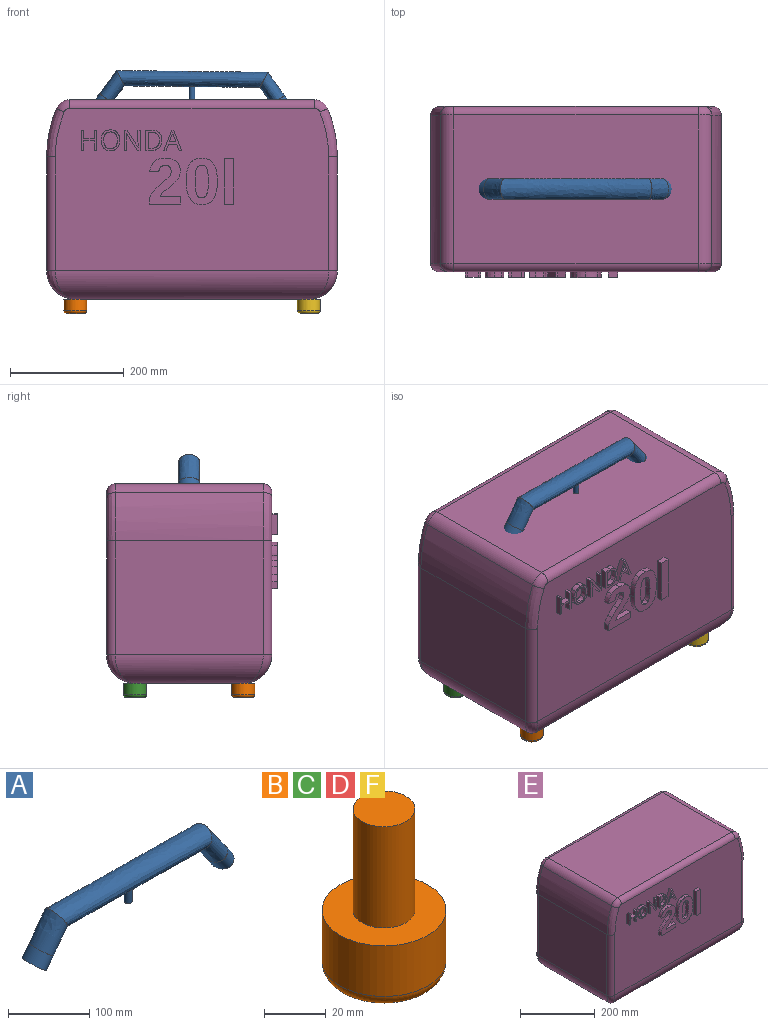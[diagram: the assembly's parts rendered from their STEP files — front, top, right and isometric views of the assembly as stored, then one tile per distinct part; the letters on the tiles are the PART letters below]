
ASSEMBLY  parts=6 mates=5
PART A: 9 faces, bbox 359.2x36.4x84.2 mm
  f0: bspline ~265.3x36.21mm, area 25120.1mm2, adj f3,f5,f7
  f1: plane 36.39x21.71mm, normal (0.59,0,-0.81), area 769.4mm2, adj f4
  f2: plane 36.39x21.24mm, normal (-0.61,0,-0.79), area 769.4mm2, adj f6
  f3: bspline ~56.62x50.7mm, area 4362mm2, adj f0,f4
  f4: bspline ~55.05x48.1mm, area 2003.3mm2, adj f1,f3
  f5: bspline ~56.89x52.04mm, area 4384.8mm2, adj f0,f6
  f6: bspline ~36.21x33.59mm, area 2002mm2, adj f2,f5
  f7: cylinder r=5mm len=23.14mm, axis (0,0,-1), area 727mm2, adj f0,f8
  f8: plane 10x10mm, normal (0,0,-1), area 78.5mm2, adj f7
PART B: 6 faces, bbox 43.3x43.3x65 mm
  f0: cylinder r=20mm len=40mm, axis (0,0,1), area 2513.3mm2, adj f2,f5
  f1: plane 30x30mm, normal (0,0,-1), area 706.9mm2, adj f5
  f2: plane 40x40mm, normal (0,0,1), area 942.5mm2, adj f0,f3
  f3: cylinder r=10mm len=40mm, axis (0,0,-1), area 2513.3mm2, adj f2,f4
  f4: plane 20x20mm, normal (0,0,1), area 314.2mm2, adj f3
  f5: torus R=15mm, axis (0,0,1), area 897.3mm2, adj f0,f1
PART C: same geometry as B
PART D: same geometry as B
PART E: 160 faces, bbox 510x300x350 mm
  f0: plane 260x200mm, normal (1,0,0), area 52000mm2, adj f3,f6,f15,f30
  f1: plane 429.9x260mm, normal (0,0,1), area 111772.7mm2, adj f10,f11,f18,f27
  f2: plane 260x200mm, normal (-1,0,0), area 52000mm2, adj f4,f7,f21,f24
  f3: extruded ~260x84.59mm, area 22577.4mm2, adj f0,f10,f16,f29
  f4: extruded ~260x84.59mm, area 22577.4mm2, adj f2,f11,f20,f25
  f5: plane 410x190mm, normal (0,0,-1), area 77900mm2, adj f6,f7,f9,f13
  f6: cylinder r=50mm len=260mm, axis (0,-1,0), area 18422.6mm2, adj f0,f5,f14,f31
  f7: cylinder r=50mm len=260mm, axis (0,1,0), area 18422.6mm2, adj f2,f5,f22,f23
  f8: plane 480x285mm, normal (0,1,0), area 135753.4mm2, adj f9,f24,f25,f26,f27,f28,f29,f30
  f9: cylinder r=50mm len=480mm, axis (1,0,0), area 35701.3mm2, adj f5,f8,f23,f31
  f10: cylinder r=25mm len=260mm, axis (0,1,0), area 7651mm2, adj f1,f3,f17,f28
  f11: cylinder r=25mm len=260mm, axis (0,1,0), area 7651mm2, adj f1,f4,f19,f26
  f12: plane 480x285mm, normal (0,-1,0), area 125242.9mm2, adj f13,f15,f16,f17,f18,f19,f20,f21
  f13: cylinder r=50mm len=480mm, axis (1,0,0), area 35701.3mm2, adj f5,f12,f14,f22
  f14: bspline ~58.44x50mm, area 1261.4mm2, adj f6,f13,f15
  f15: cylinder r=15mm len=200mm, axis (0,0,1), area 4712.4mm2, adj f0,f12,f14,f16
  f16: bspline ~109.39x35.94mm, area 1995.5mm2, adj f3,f12,f15,f17
  f17: torus R=10mm, axis (0,1,0), area 542.2mm2, adj f10,f12,f16,f18
  f18: cylinder r=15mm len=429.9mm, axis (-1,0,0), area 10129.2mm2, adj f1,f12,f17,f19
  f19: torus R=10mm, axis (0,1,0), area 542.2mm2, adj f11,f12,f18,f20
  f20: bspline ~109.39x35.94mm, area 1995.5mm2, adj f4,f12,f19,f21
  f21: cylinder r=15mm len=200mm, axis (0,0,-1), area 4712.4mm2, adj f2,f12,f20,f22
  f22: bspline ~58.44x50mm, area 1261.4mm2, adj f7,f13,f21
  f23: bspline ~58.44x50mm, area 1261.4mm2, adj f7,f9,f24
  f24: cylinder r=15mm len=200mm, axis (0,0,-1), area 4712.4mm2, adj f2,f8,f23,f25
  f25: bspline ~109.39x35.94mm, area 1995.5mm2, adj f4,f8,f24,f26
  f26: torus R=10mm, axis (0,-1,0), area 542.2mm2, adj f8,f11,f25,f27
  f27: cylinder r=15mm len=429.9mm, axis (-1,0,0), area 10129.2mm2, adj f1,f8,f26,f28
  f28: torus R=10mm, axis (0,-1,0), area 542.2mm2, adj f8,f10,f27,f29
  f29: bspline ~109.39x35.94mm, area 1995.5mm2, adj f3,f8,f28,f30
  f30: cylinder r=15mm len=200mm, axis (0,0,1), area 4712.4mm2, adj f0,f8,f29,f31
  f31: bspline ~58.44x50mm, area 1261.4mm2, adj f6,f9,f30
  f32: plane 35.58x10mm, normal (1,0,0), area 355.8mm2, adj f12,f33,f43,f44
  f33: plane 10x4.14mm, normal (0,0,1), area 41.4mm2, adj f12,f32,f34,f44
  f34: plane 15.14x10mm, normal (-1,0,0), area 151.4mm2, adj f12,f33,f35,f44
  f35: plane 18.74x10mm, normal (0,0,1), area 187.4mm2, adj f12,f34,f36,f44
  f36: plane 15.14x10mm, normal (1,0,0), area 151.4mm2, adj f12,f35,f37,f44
  f37: plane 10x4.14mm, normal (0,0,1), area 41.4mm2, adj f12,f36,f38,f44
  f38: plane 35.58x10mm, normal (-1,0,0), area 355.8mm2, adj f12,f37,f39,f44
  f39: plane 10x4.14mm, normal (0,0,-1), area 41.4mm2, adj f12,f38,f40,f44
  f40: plane 16.74x10mm, normal (1,0,0), area 167.4mm2, adj f12,f39,f41,f44
  f41: plane 18.74x10mm, normal (0,0,-1), area 187.4mm2, adj f12,f40,f42,f44
  f42: plane 16.74x10mm, normal (-1,0,0), area 167.4mm2, adj f12,f41,f43,f44
  f43: plane 10x4.14mm, normal (0,0,-1), area 41.4mm2, adj f12,f32,f42,f44
  f44: plane 35.58x27.01mm, normal (0,-1,0), area 363.6mm2, adj f32,f33,f34,f35,f36,f37,f38,f39
  f45: extruded ~13.43x10mm, area 144.3mm2, adj f12,f46,f60,f61
  f46: extruded ~11.98x10mm, area 133.5mm2, adj f12,f45,f47,f61
  f47: extruded ~12.16x10mm, area 134.9mm2, adj f12,f46,f48,f61
  f48: extruded ~13.47x10mm, area 144.6mm2, adj f12,f47,f49,f61
  f49: extruded ~13.57x10mm, area 145.5mm2, adj f12,f48,f50,f61
  f50: extruded ~12.13x10mm, area 134.7mm2, adj f12,f49,f51,f61
  f51: extruded ~12.01x10mm, area 133.9mm2, adj f12,f50,f60,f61
  f52: extruded ~10.86x10mm, area 115.2mm2, adj f53,f59,f61,f62
  f53: extruded ~10x8.99mm, area 100.8mm2, adj f52,f54,f61,f62
  f54: extruded ~10x8.89mm, area 99.8mm2, adj f53,f55,f61,f62
  f55: extruded ~10.89x10mm, area 115.2mm2, adj f54,f56,f61,f62
  f56: extruded ~10.98x10mm, area 116.1mm2, adj f55,f57,f61,f62
  f57: extruded ~10x8.93mm, area 100.2mm2, adj f56,f58,f61,f62
  f58: extruded ~10x8.94mm, area 100.4mm2, adj f57,f59,f61,f62
  f59: extruded ~10.96x10mm, area 116.1mm2, adj f52,f58,f61,f62
  f60: extruded ~13.44x10mm, area 144.4mm2, adj f12,f45,f51,f61
  f61: plane 36.63x32.73mm, normal (0,-1,0), area 400.6mm2, adj f45,f46,f47,f48,f49,f50,f51,f52
  f62: plane 29.3x23.97mm, normal (0,-1,0), area 582.3mm2, adj f52,f53,f54,f55,f56,f57,f58,f59
  f63: plane 35.58x10mm, normal (1,0,0), area 355.8mm2, adj f12,f64,f77,f78
  f64: plane 10x3.87mm, normal (0,0,1), area 38.7mm2, adj f12,f63,f65,f78
  f65: plane 20.42x10mm, normal (-1,0,0), area 204.2mm2, adj f12,f64,f66,f78
  f66: extruded ~10x5.1mm, area 51mm2, adj f12,f65,f67,f78
  f67: extruded ~10x4.22mm, area 42.3mm2, adj f12,f66,f68,f78
  f68: plane 10x0.19mm, normal (0,0,1), area 1.9mm2, adj f12,f67,f69,f78
  f69: plane 29.74x19.4mm, normal (0.84,0,0.55), area 355.1mm2, adj f12,f68,f70,f78
  f70: plane 10x4.67mm, normal (0,0,1), area 46.7mm2, adj f12,f69,f71,f78
  f71: plane 35.58x10mm, normal (-1,0,0), area 355.8mm2, adj f12,f70,f72,f78
  f72: plane 10x3.82mm, normal (0,0,-1), area 38.2mm2, adj f12,f71,f73,f78
  f73: plane 20.22x10mm, normal (1,0,0), area 202.2mm2, adj f12,f72,f74,f78
  f74: extruded ~10x9.63mm, area 96.4mm2, adj f12,f73,f75,f78
  f75: plane 10x0.19mm, normal (0,0,-1), area 1.9mm2, adj f12,f74,f76,f78
  f76: plane 29.86x19.45mm, normal (-0.84,0,-0.55), area 356.3mm2, adj f12,f75,f77,f78
  f77: plane 10x4.72mm, normal (0,0,-1), area 47.2mm2, adj f12,f63,f76,f78
  f78: plane 35.58x27.79mm, normal (0,-1,0), area 417.9mm2, adj f63,f64,f65,f66,f67,f68,f69,f70
  f79: extruded ~12.85x10mm, area 140.2mm2, adj f12,f80,f92,f93
  f80: extruded ~12.9x10mm, area 140.7mm2, adj f12,f79,f81,f93
  f81: plane 10.9x10mm, normal (0,0,1), area 109mm2, adj f12,f80,f82,f93
  f82: plane 35.58x10mm, normal (-1,0,0), area 355.8mm2, adj f12,f81,f83,f93
  f83: plane 10x9.86mm, normal (0,0,-1), area 98.6mm2, adj f12,f82,f84,f93
  f84: extruded ~13.76x10mm, area 149.1mm2, adj f12,f83,f92,f93
  f85: extruded ~10.77x10mm, area 117.1mm2, adj f86,f91,f93,f94
  f86: extruded ~11.12x10mm, area 120.1mm2, adj f85,f87,f93,f94
  f87: plane 10x5.04mm, normal (0,0,1), area 50.4mm2, adj f86,f88,f93,f94
  f88: plane 28.42x10mm, normal (1,0,0), area 284.2mm2, adj f87,f89,f93,f94
  f89: plane 10x6.01mm, normal (0,0,-1), area 60.1mm2, adj f88,f90,f93,f94
  f90: extruded ~10.38x10mm, area 112.6mm2, adj f89,f91,f93,f94
  f91: extruded ~10.49x10mm, area 113.5mm2, adj f85,f90,f93,f94
  f92: extruded ~13.47x10mm, area 146.9mm2, adj f12,f79,f84,f93
  f93: plane 35.58x28.4mm, normal (0,-1,0), area 400.4mm2, adj f79,f80,f81,f82,f83,f84,f85,f86
  f94: plane 28.42x19.89mm, normal (0,-1,0), area 496.5mm2, adj f85,f86,f87,f88,f89,f90,f91
  f95: plane 10x4.28mm, normal (0,0,-1), area 42.8mm2, adj f12,f96,f107,f108
  f96: plane 35.73x13.99mm, normal (0.93,0,0.36), area 383.7mm2, adj f12,f95,f97,f108
  f97: plane 10x3.48mm, normal (0,0,1), area 34.8mm2, adj f12,f96,f98,f108
  f98: plane 35.73x14.06mm, normal (-0.93,0,0.37), area 384mm2, adj f12,f97,f99,f108
  f99: plane 10x4.19mm, normal (0,0,-1), area 41.9mm2, adj f12,f98,f100,f108
  f100: plane 11.32x10mm, normal (0.93,0,-0.36), area 121.3mm2, adj f12,f99,f101,f108
  f101: plane 14.26x10mm, normal (0,0,-1), area 142.6mm2, adj f12,f100,f107,f108
  f102: plane 11.51x10mm, normal (0,0,1), area 115.1mm2, adj f103,f106,f108,f109
  f103: plane 11.03x10mm, normal (0.94,0,-0.35), area 117.9mm2, adj f102,f104,f108,f109
  f104: extruded ~10x5.13mm, area 53.6mm2, adj f103,f105,f108,f109
  f105: extruded ~10x5.13mm, area 53.9mm2, adj f104,f106,f108,f109
  f106: plane 11.03x10mm, normal (-0.94,0,-0.35), area 117.8mm2, adj f102,f105,f108,f109
  f107: plane 11.32x10mm, normal (-0.93,0,-0.36), area 121.5mm2, adj f12,f95,f101,f108
  f108: plane 35.73x31.54mm, normal (0,-1,0), area 325.7mm2, adj f95,f96,f97,f98,f99,f100,f101,f102
  f109: plane 16.16x11.51mm, normal (0,-1,0), area 88.7mm2, adj f102,f103,f104,f105,f106
  f110: plane 55.43x10mm, normal (0,0,-1), area 554.3mm2, adj f12,f111,f131,f132
  f111: plane 12.99x10mm, normal (1,0,0), area 129.9mm2, adj f12,f110,f112,f132
  f112: plane 36.77x10mm, normal (0,0,1), area 367.7mm2, adj f12,f111,f113,f132
  f113: extruded ~10x6.85mm, area 84.3mm2, adj f12,f112,f114,f132
  f114: extruded ~10x7.17mm, area 95.8mm2, adj f12,f113,f115,f132
  f115: extruded ~10x8.12mm, area 103.8mm2, adj f12,f114,f116,f132
  f116: extruded ~10x7.62mm, area 104.4mm2, adj f12,f115,f117,f132
  f117: extruded ~10x8.29mm, area 100.5mm2, adj f12,f116,f118,f132
  f118: extruded ~10.06x10mm, area 103.8mm2, adj f12,f117,f119,f132
  f119: extruded ~16.43x10mm, area 184.1mm2, adj f12,f118,f120,f132
  f120: extruded ~19.68x10mm, area 209.7mm2, adj f12,f119,f121,f132
  f121: extruded ~18.75x10mm, area 200.4mm2, adj f12,f120,f122,f132
  f122: extruded ~16.8x10mm, area 191.8mm2, adj f12,f121,f123,f132
  f123: plane 15.92x10mm, normal (-0.06,0,-1), area 159.5mm2, adj f12,f122,f124,f132
  f124: extruded ~10x8.18mm, area 90.2mm2, adj f12,f123,f125,f132
  f125: extruded ~10x7.74mm, area 84.3mm2, adj f12,f124,f126,f132
  f126: extruded ~10.4x10.35mm, area 168.4mm2, adj f12,f125,f127,f132
  f127: extruded ~10x8.61mm, area 94.1mm2, adj f12,f126,f128,f132
  f128: extruded ~11.68x11.13mm, area 161.6mm2, adj f12,f127,f129,f132
  f129: extruded ~14.36x13.49mm, area 197.2mm2, adj f12,f128,f130,f132
  f130: extruded ~13.28x10mm, area 159.9mm2, adj f12,f129,f131,f132
  f131: plane 10.96x10mm, normal (-1,0,0), area 109.6mm2, adj f12,f110,f130,f132
  f132: plane 80.4x55.43mm, normal (0,-1,0), area 2384.7mm2, adj f110,f111,f112,f113,f114,f115,f116,f117
  f133: extruded ~30.59x10mm, area 316.8mm2, adj f12,f134,f152,f153
  f134: extruded ~20.57x10.17mm, area 240.4mm2, adj f12,f133,f135,f153
  f135: extruded ~15.75x10mm, area 165.9mm2, adj f12,f134,f136,f153
  f136: extruded ~13.27x10mm, area 162.7mm2, adj f12,f135,f137,f153
  f137: extruded ~23.23x10mm, area 235.1mm2, adj f12,f136,f138,f153
  f138: extruded ~40.77x27.22mm, area 556.1mm2, adj f12,f137,f139,f153
  f139: extruded ~20.65x10.35mm, area 241.6mm2, adj f12,f138,f152,f153
  f140: extruded ~16.63x10mm, area 166.9mm2, adj f141,f151,f153,f154
  f141: extruded ~10x8.91mm, area 97mm2, adj f140,f142,f153,f154
  f142: extruded ~10x6.94mm, area 77.3mm2, adj f141,f143,f153,f154
  f143: extruded ~10x6.94mm, area 76.6mm2, adj f142,f144,f153,f154
  f144: extruded ~10x8.74mm, area 95.3mm2, adj f143,f145,f153,f154
  f145: extruded ~16.95x10mm, area 170mm2, adj f144,f146,f153,f154
  f146: extruded ~17.01x10mm, area 170.6mm2, adj f145,f147,f153,f154
  f147: extruded ~10x8.71mm, area 95mm2, adj f146,f148,f153,f154
  f148: extruded ~10x7.21mm, area 79.3mm2, adj f147,f149,f153,f154
  f149: extruded ~10x6.86mm, area 75.8mm2, adj f148,f150,f153,f154
  f150: extruded ~10x8.71mm, area 94.7mm2, adj f149,f151,f153,f154
  f151: extruded ~17.05x10mm, area 171mm2, adj f140,f150,f153,f154
  f152: extruded ~30.41x10mm, area 316.2mm2, adj f12,f133,f139,f153
  f153: plane 81.54x54.77mm, normal (0,-1,0), area 2598.9mm2, adj f133,f134,f135,f136,f137,f138,f139,f140
  f154: plane 56.73x23.12mm, normal (0,-1,0), area 1137.1mm2, adj f140,f141,f142,f143,f144,f145,f146,f147
  f155: plane 16.59x10mm, normal (0,0,-1), area 165.9mm2, adj f12,f156,f158,f159
  f156: plane 79.22x10mm, normal (1,0,0), area 792.2mm2, adj f12,f155,f157,f159
  f157: plane 16.59x10mm, normal (0,0,1), area 165.9mm2, adj f12,f156,f158,f159
  f158: plane 79.22x10mm, normal (-1,0,0), area 792.2mm2, adj f12,f155,f157,f159
  f159: plane 79.22x16.59mm, normal (0,-1,0), area 1314mm2, adj f155,f156,f157,f158
PART F: same geometry as B
PLACE A t=(-243.46,-56.64,300.88)mm
PLACE B t=(-448.46,-151.64,-49.12)mm
PLACE C t=(-448.46,38.36,-49.12)mm
PLACE D t=(-38.46,38.36,-49.12)mm
PLACE E t=(-243.46,-56.64,100.88)mm fixed
PLACE F t=(-38.46,-151.64,-49.12)mm
MATE fastened A.f7 <-> E.f1  axis (0,0,-1) through (-243.46,-56.64,300.88)mm
MATE fastened D.f3 <-> E.f5  axis (0,0,-1) through (-38.46,38.36,-49.12)mm
MATE fastened F.f3 <-> E.f5  axis (0,0,-1) through (-38.46,-151.64,-49.12)mm
MATE fastened B.f3 <-> E.f5  axis (0,0,1) through (-448.46,-151.64,-49.12)mm
MATE fastened C.f3 <-> E.f5  axis (0,0,-1) through (-448.46,38.36,-49.12)mm
